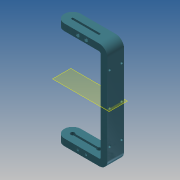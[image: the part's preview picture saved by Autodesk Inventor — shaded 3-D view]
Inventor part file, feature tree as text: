
AUTODESK INVENTOR PART (.ipt)
format: ipt  version: 2013 (Build 170138000, 138)  size: 270,336 bytes
history: native  units: mm
features: extrude x10, sketch x10, pattern_linear x2, projected_geometry x2, fillet x1, plane x1
ambient origin geometry x8: Origin, YZ Plane, XZ Plane, XY Plane, X Axis, Y Axis, Z Axis, Center Point
bodies: Solid1 (feature_tree)
feature tree (26):
  extrude  "Extrusion1"  Depth=25.0mm
  extrude  "Extrusion2"  Depth=160.0mm
  extrude  "Extrusion3"  Depth=10.0mm TaperAngle=0.0deg
  extrude  "Extrusion4"  Depth=5.0mm TaperAngle=0.0deg
  fillet  "Fillet2"  Radius=40.0mm
  extrude  "Extrusion11"  Depth=2.5mm
  extrude  "Extrusion12"  Depth=3.5mm
  extrude  "Extrusion13"  Depth=10.0mm TaperAngle=0.0deg
  extrude  "Extrusion14"  Depth=4.0mm TaperAngle=0.0deg
  pattern_linear  "Rectangular Pattern1"  Spacing1=12.5mm  [1 undecoded]
  extrude  "Extrusion15"  Depth=3.5mm
  extrude  "Extrusion16"  Depth=10.0mm TaperAngle=0.0deg
  plane  "Work Plane1"
  pattern_linear  "Rectangular Pattern2"  Count1=2  [1 undecoded]
  sketch  "Sketch1"  dims[d0=65.0mm d2=25.0mm]
  sketch  "Sketch2"  dims[d3=10.0mm d4=0.0mm d5=160.0mm]
  sketch  "Sketch3"  dims[d6=10.0mm d7=0.0mm d8=10.0mm d9=0.0mm]
  projected_geometry  "Projected Loop1"
  sketch  "Sketch4"  dims[d10=6.0mm d12=5.0mm d13=0.0mm d14=40.0mm]
  sketch  "Sketch11"  dims[d15=150.0mm d16=0.0mm d41=2.5mm d42=12.5mm]
  projected_geometry  "Projected Loop2"
  sketch  "Sketch12"  dims[d49=20.0mm d50=3.5mm]
  sketch  "Sketch13"  dims[d51=18.0mm d52=10.0mm d53=0.0mm]
  sketch  "Sketch14"  dims[d54=5.5mm d55=4.0mm d56=0.0mm]
  sketch  "Sketch15"  dims[d57=3.0mm]
  sketch  "Sketch16"  dims[d59=10.0mm d60=0.0mm d61=12.5mm d63=3.5mm d65=10.0mm d66=0.0mm d67=20.0mm d69=150.0mm d70=5.5mm d71=4.0mm d72=0.0mm d73=5.5mm d74=4.0mm d75=0.0mm d76=30.0mm d78=50.0mm d79=15.625mm]
note: 2 required parameter values undecoded (feature->parameter linkage not recoverable at this tier; creation-order binding heuristic only, values carry confidence <= 0.55)
